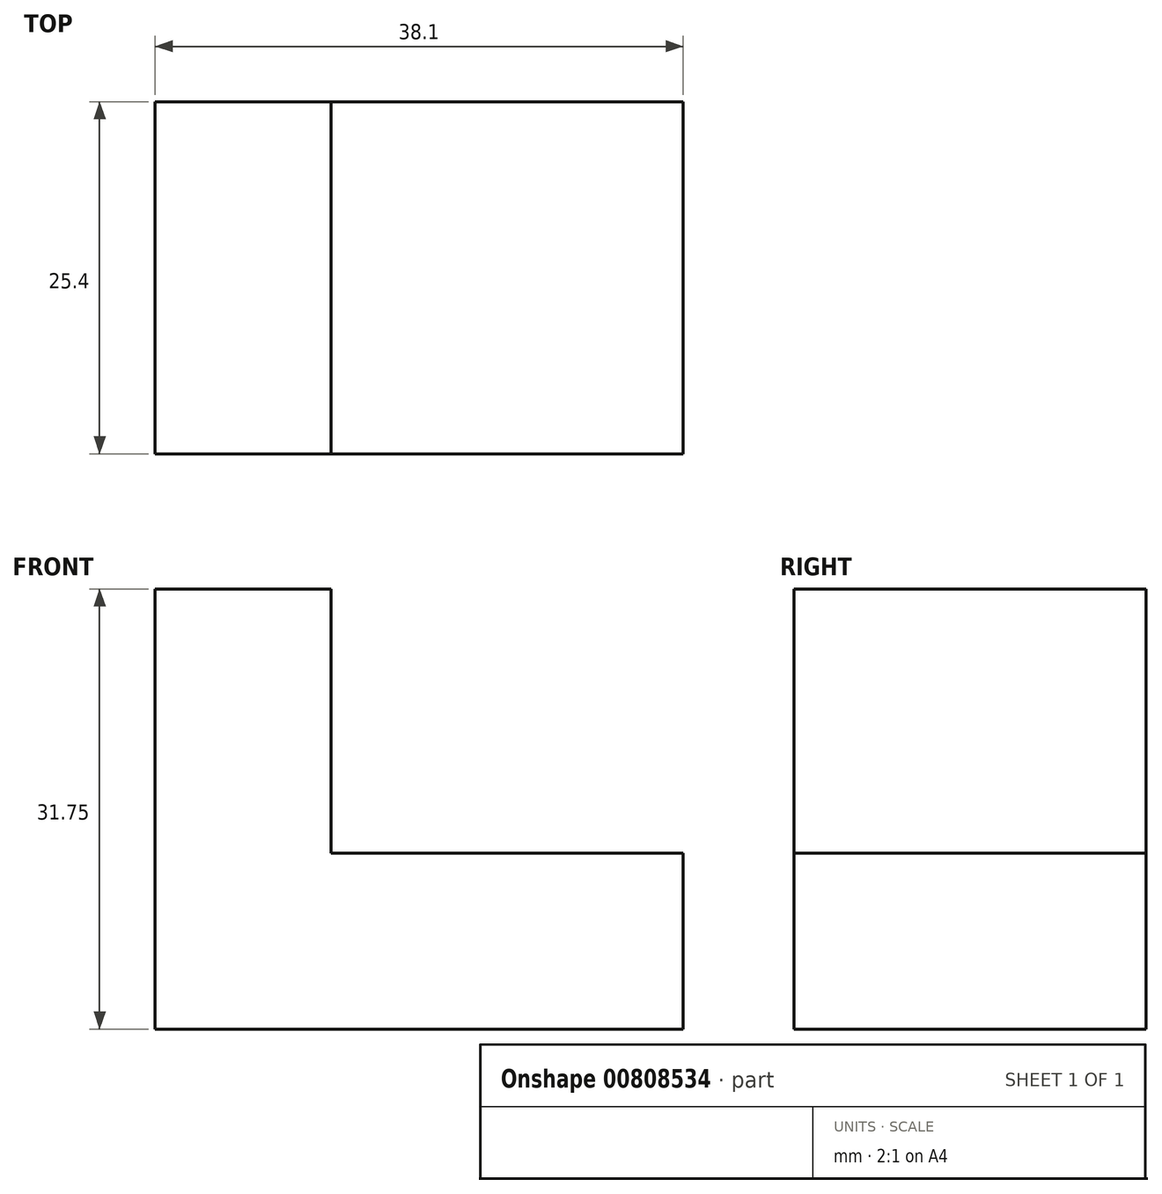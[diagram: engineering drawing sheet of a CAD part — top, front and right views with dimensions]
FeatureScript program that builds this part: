
annotation { "Feature Type Name" : "Feature", "Feature Type Description" : "" }
export const myFeature = defineFeature(function(context is Context, id is Id, definition is map)
    precondition{}
    {
        {
            var Q0;
            Q0=qCreatedBy(makeId("Front.planeOp"),FACE);
            var sketch = newSketch(context, id + "F0", { "sketchPlane" : qUnion([Q0])});
            skLineSegment(sketch, "E0", {"start": v(0, 0) * mm, "end": v(0, 31.75) * mm});
            skLineSegment(sketch, "E1", {"start": v(0, 31.75) * mm, "end": v(12.7, 31.75) * mm});
            skLineSegment(sketch, "E2", {"start": v(12.7, 31.75) * mm, "end": v(12.7, 12.7) * mm});
            skLineSegment(sketch, "E3", {"start": v(12.7, 12.7) * mm, "end": v(38.1, 12.7) * mm});
            skLineSegment(sketch, "E4", {"start": v(38.1, 12.7) * mm, "end": v(38.1, 0) * mm});
            skLineSegment(sketch, "E5", {"start": v(0, 0) * mm, "end": v(38.1, 0) * mm});
            skSolve(sketch);
        }
        {
            var Q0;
            Q0 = qSketchRegion(id + "F0", true);
            extrude(context, id + "F1", {"entities" : qUnion([Q0]), "depth" : 25.4 * mm, "offsetDistance" : 25.4 * mm});
        }
    });
